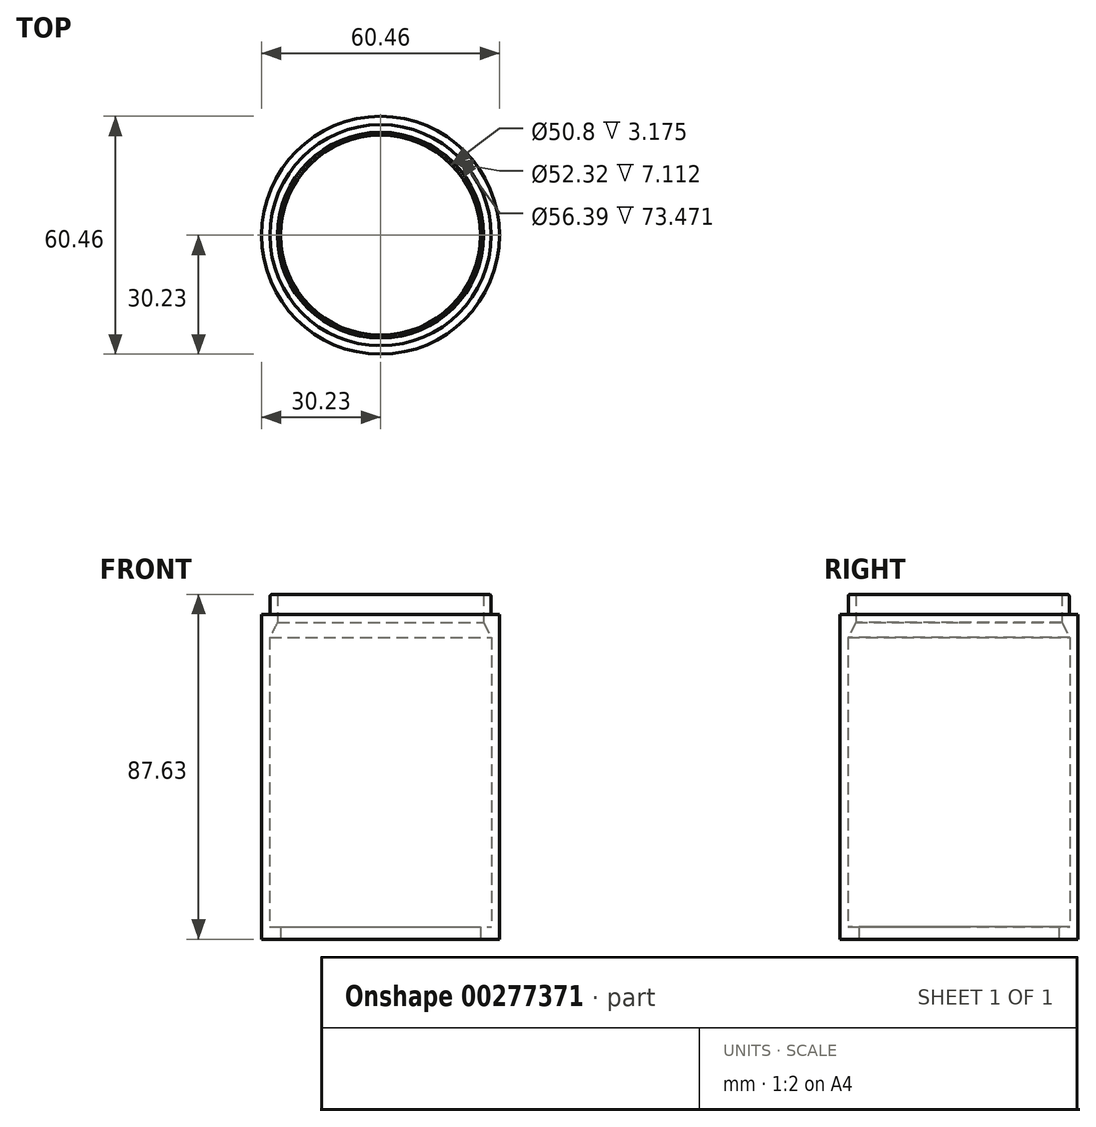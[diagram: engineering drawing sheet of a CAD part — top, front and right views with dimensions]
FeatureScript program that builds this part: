
annotation { "Feature Type Name" : "Feature", "Feature Type Description" : "" }
export const myFeature = defineFeature(function(context is Context, id is Id, definition is map)
    precondition{}
    {
        {
            var Q0;
            Q0=qCreatedBy(makeId("Top.planeOp"),FACE);
            var sketch = newSketch(context, id + "F0", { "sketchPlane" : qUnion([Q0])});
            skCircle(sketch, "E0", {"center": v(0, 0) * mm, "radius": 30.23 * mm});
            skCircle(sketch, "E1", {"center": v(0, 0) * mm, "radius": 25.4 * mm});
            skSolve(sketch);
        }
        {
            var Q0;
            Q0 = qSketchRegion(id + "F0", true);
            extrude(context, id + "F1", {"entities" : qUnion([Q0]), "depth" : 82.55 * mm});
        }
        {
            var Q0;
            Q0=qCreatedBy(makeId("Right.planeOp"),FACE);
            var sketch = newSketch(context, id + "F2", { "sketchPlane" : qUnion([Q0]), "disableImprinting" : false});
            skLineSegment(sketch, "E2", {"start": v(0, 0) * mm, "end": v(0, 3.17) * mm});
            skLineSegment(sketch, "E3", {"start": v(0, 3.18) * mm, "end": v(-28.2, 3.17) * mm});
            skLineSegment(sketch, "E4", {"start": v(-28.2, 3.17) * mm, "end": v(-28.2, 76.65) * mm});
            skLineSegment(sketch, "E5", {"start": v(-28.2, 76.65) * mm, "end": v(-26.16, 80.52) * mm});
            skLineSegment(sketch, "E6", {"start": v(0, 80.52) * mm, "end": v(0, 3.17) * mm});
            skPoint(sketch, "E7.start.orphan", {"position": v(-25.1, 82.55) * mm});
            skPoint(sketch, "E8.orphan", {"position": v(0, 82.55) * mm});
            skLineSegment(sketch, "E9", {"start": v(-26.16, 80.52) * mm, "end": v(-26.16, 83.57) * mm});
            skLineSegment(sketch, "E10", {"start": v(-26.16, 83.57) * mm, "end": v(0, 83.57) * mm});
            skLineSegment(sketch, "E11", {"start": v(0, 83.57) * mm, "end": v(0, 80.52) * mm});
            skSolve(sketch);
        }
        {
            var Q0;
            Q0 = qSketchRegion(id + "F2", true);
            var Q1;
            Q1=sQuery(id+"F2.wireOp",EDGE,"E6");
            revolve(context, id + "F3", {"operationType" : NewBodyOperationType.REMOVE, "entities" : qUnion([Q0]), "axis" : qUnion([Q1]), "revolveType" : RevolveType.FULL, "oppositeDirection" : true});
        }
        {
            var Q0;
            Q0=makeQuery(id+"F1.opExtrude","CAP_FACE",FACE,{"disambiguationData":[OSD([sQuery(id+"F0.wireOp",EDGE,"E0"),sQuery(id+"F0.wireOp",EDGE,"E1")])],"isStart":false});
            var sketch = newSketch(context, id + "F4", { "sketchPlane" : qUnion([Q0])});
            skCircle(sketch, "E12", {"center": v(0, 0) * mm, "radius": 26.16 * mm});
            skCircle(sketch, "E13", {"center": v(0, 0) * mm, "radius": 28.07 * mm});
            skSolve(sketch);
        }
        {
            var Q0;
            Q0 = qSketchRegion(id + "F4", true);
            extrude(context, id + "F5", {"entities" : qUnion([Q0]), "operationType" : NewBodyOperationType.ADD, "depth" : 5.08 * mm});
        }
        {
            var Q0;
            Q0=makeQuery(id+"F5.opExtrude","CAP_EDGE",EDGE,{"disambiguationData":[OSD([sQuery(id+"F4.wireOp",EDGE,"E13")])],"isStart":false});
            fillet(context, id + "F6", {"entities" : qUnion([Q0]), "radius" : 0.5 * mm, "tangentPropagation" : true, "allowEdgeOverflow" : false});
        }
    });
